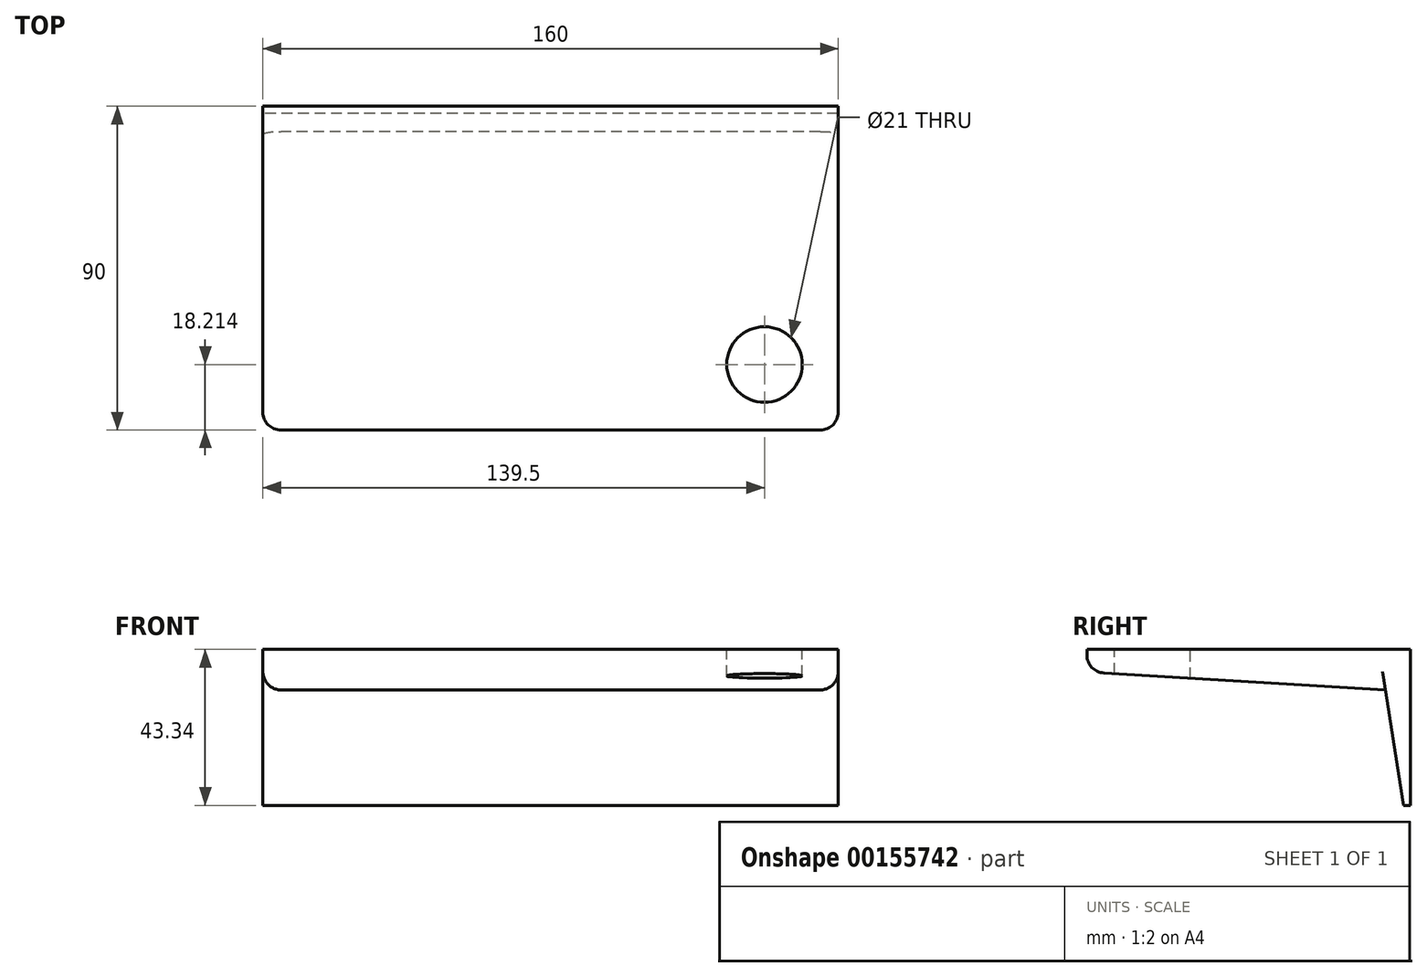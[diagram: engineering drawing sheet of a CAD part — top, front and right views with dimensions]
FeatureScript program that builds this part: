
annotation { "Feature Type Name" : "Feature", "Feature Type Description" : "" }
export const myFeature = defineFeature(function(context is Context, id is Id, definition is map)
    precondition{}
    {
        {
            var Q0;
            Q0=qCreatedBy(makeId("Right.planeOp"),FACE);
            var sketch = newSketch(context, id + "F0", { "sketchPlane" : qUnion([Q0])});
            skLineSegment(sketch, "E0", {"start": v(-34.87, 22.79) * mm, "end": v(55.13, 22.79) * mm});
            skLineSegment(sketch, "E1", {"start": v(55.13, 22.79) * mm, "end": v(55.13, -20.55) * mm});
            skLineSegment(sketch, "E2", {"start": v(55.13, -20.55) * mm, "end": v(53.13, -20.55) * mm});
            skLineSegment(sketch, "E3", {"start": v(53.13, -20.55) * mm, "end": v(48.13, 11.54) * mm});
            skLineSegment(sketch, "E4", {"start": v(48.13, 11.54) * mm, "end": v(-34.87, 16.54) * mm});
            skLineSegment(sketch, "E5", {"start": v(-34.87, 16.54) * mm, "end": v(-34.87, 22.79) * mm});
            skSolve(sketch);
        }
        {
            var Q0;
            Q0 = qSketchRegion(id + "F0", true);
            extrude(context, id + "F1", {"entities" : qUnion([Q0]), "endBound" : BoundingType.SYMMETRIC, "depth" : 160 * mm});
        }
        {
            var Q0;
            Q0=makeQuery(id+"F1.opExtrude","SWEPT_FACE",FACE,{"disambiguationData":[OSD([sQuery(id+"F0.wireOp",EDGE,"E0")])]});
            var sketch = newSketch(context, id + "F2", { "sketchPlane" : qUnion([Q0])});
            skCircle(sketch, "E6", {"center": v(59.5, -16.66) * mm, "radius": 10.5 * mm});
            skSolve(sketch);
        }
        {
            var Q0;
            Q0=makeQuery(id+"F2.imprint","IMPRINT",FACE,{"disambiguationData":[TD([[makeQuery(id+"F2.imprint","IMPRINT",EDGE,{"derivedFrom":sQuery(id+"F2.wireOp",EDGE,"E6")}),1.0]])]});
            var Q1;
            Q1=sQuery(id+"F2.wireOp",EDGE,"E6");
            extrude(context, id + "F3", {"entities" : qUnion([Q0]), "operationType" : NewBodyOperationType.REMOVE, "surfaceEntities" : qUnion([Q1]), "oppositeDirection" : true, "depth" : 25 * mm});
        }
        {
            var Q0;
            Q0=makeQuery(id+"F1.opExtrude","CAP_EDGE",EDGE,{"disambiguationData":[OSD([sQuery(id+"F0.wireOp",EDGE,"E5")])],"isStart":false});
            var Q1;
            Q1=makeQuery(id+"F1.opExtrude","CAP_EDGE",EDGE,{"disambiguationData":[OSD([sQuery(id+"F0.wireOp",EDGE,"E5")])],"isStart":true});
            var Q2;
            Q2=makeQuery(id+"F1.opExtrude","CAP_EDGE",EDGE,{"disambiguationData":[OSD([sQuery(id+"F0.wireOp",EDGE,"E4")])],"isStart":false});
            var Q3;
            Q3=makeQuery(id+"F1.opExtrude","CAP_EDGE",EDGE,{"disambiguationData":[OSD([sQuery(id+"F0.wireOp",EDGE,"E4")])],"isStart":true});
            var Q4;
            Q4=makeQuery(id+"F1.opExtrude","SWEPT_EDGE",EDGE,{"disambiguationData":[OSD([sQuery(id+"F0.wireOp",EDGE,"E4"),sQuery(id+"F0.wireOp",EDGE,"E5")])]});
            fillet(context, id + "F4", {"entities" : qUnion([Q0, Q1, Q2, Q3, Q4]), "radius" : 5 * mm, "tangentPropagation" : true, "allowEdgeOverflow" : false});
        }
    });
